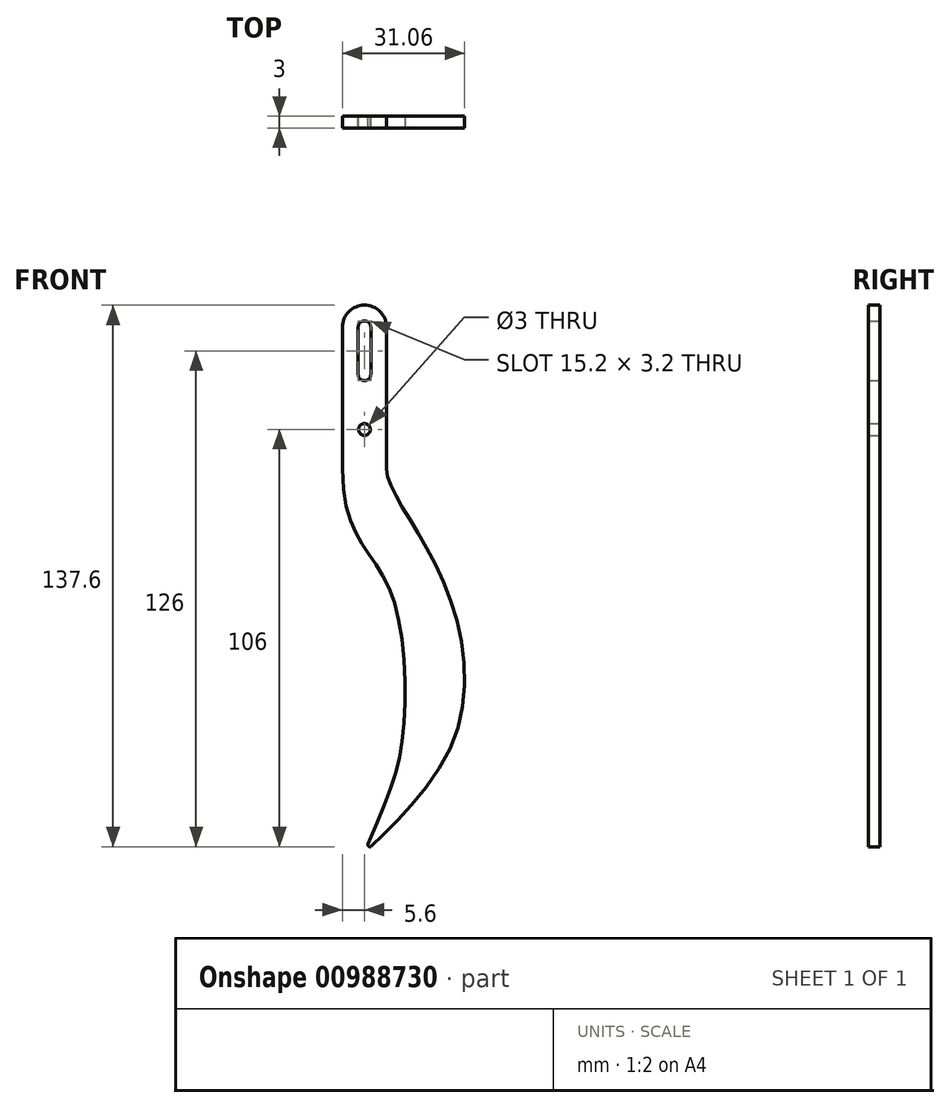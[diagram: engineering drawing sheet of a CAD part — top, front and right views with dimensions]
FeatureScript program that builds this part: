
annotation { "Feature Type Name" : "Feature", "Feature Type Description" : "" }
export const myFeature = defineFeature(function(context is Context, id is Id, definition is map)
    precondition{}
    {
        {
            var Q0;
            Q0=qCreatedBy(makeId("Front.planeOp"),FACE);
            var sketch = newSketch(context, id + "F0", { "sketchPlane" : qUnion([Q0])});
            skLineSegment(sketch, "E0", {"start": v(-7.2, 24) * mm, "end": v(-7.2, 36) * mm});
            skLineSegment(sketch, "E1", {"start": v(-4, 36) * mm, "end": v(-4, 24) * mm});
            skArc(sketch, "E2", {"start": v(-4, 36) * mm, "mid": v(-5.6, 37.6) * mm, "end": v(-7.2, 36) * mm});
            skArc(sketch, "E3", {"start": v(-7.2, 24) * mm, "mid": v(-5.6, 22.4) * mm, "end": v(-4, 24) * mm});
            skArc(sketch, "E4", {"start": v(0, 36) * mm, "mid": v(-5.6, 41.6) * mm, "end": v(-11.2, 36) * mm});
            skLineSegment(sketch, "E5", {"start": v(-11.2, 36) * mm, "end": v(-11.2, 0) * mm});
            skLineSegment(sketch, "E6", {"start": v(0, 36) * mm, "end": v(0, 0) * mm});
            skCircle(sketch, "E7", {"center": v(-5.6, 10) * mm, "radius": 1.5 * mm});
            skLineSegment(sketch, "E8", {"start": v(-5.6, -25) * mm, "end": v(-5.6, 10) * mm, "construction": true});
            skLineSegment(sketch, "E9", {"start": v(-5.6, -25) * mm, "end": v(-5.6, -97.5) * mm, "construction": true});
            skLineSegment(sketch, "E10", {"start": v(-11.2, 0) * mm, "end": v(0, 0) * mm});
            skFitSpline(sketch, "E11", {"points": [v(-5.6, -97.5) * mm, v(4, -69) * mm, v(2, -34) * mm, v(-5.6, -20) * mm, v(-11.2, 0) * mm], "startDerivative": vector(61.13, 147.24) * mm, "endDerivative": vector(0, 131.35) * mm});
            skFitSpline(sketch, "E12", {"points": [v(0, 0) * mm, v(3, -8) * mm, v(15, -30) * mm, v(17, -69) * mm, v(-5.6, -97.5) * mm], "startDerivative": vector(0, -41.48) * mm, "endDerivative": vector(-56.3, -54) * mm});
            skSolve(sketch);
        }
        {
            var Q0;
            Q0=makeQuery(id+"F0.imprint","IMPRINT",FACE,{"disambiguationData":[TD([[makeQuery(id+"F0.imprint","IMPRINT",EDGE,{"derivedFrom":sQuery(id+"F0.wireOp",EDGE,"E0")}),1.0]])]});
            var Q1;
            Q1=makeQuery(id+"F0.imprint","IMPRINT",FACE,{"disambiguationData":[TD([[makeQuery(id+"F0.imprint","IMPRINT",EDGE,{"derivedFrom":sQuery(id+"F0.wireOp",EDGE,"E10")}),-1.0]])]});
            extrude(context, id + "F1", {"entities" : qUnion([Q0, Q1]), "depth" : 3 * mm, "offsetDistance" : 25 * mm});
        }
        {
            var Q0;
            Q0=makeQuery(id+"F1.opExtrude","SWEPT_EDGE",EDGE,{"disambiguationData":[OSD([sQuery(id+"F0.wireOp",EDGE,"E11"),sQuery(id+"F0.wireOp",EDGE,"E12")])]});
            fillet(context, id + "F2", {"entities" : qUnion([Q0]), "radius" : .5 * mm, "tangentPropagation" : true, "allowEdgeOverflow" : false});
        }
    });
